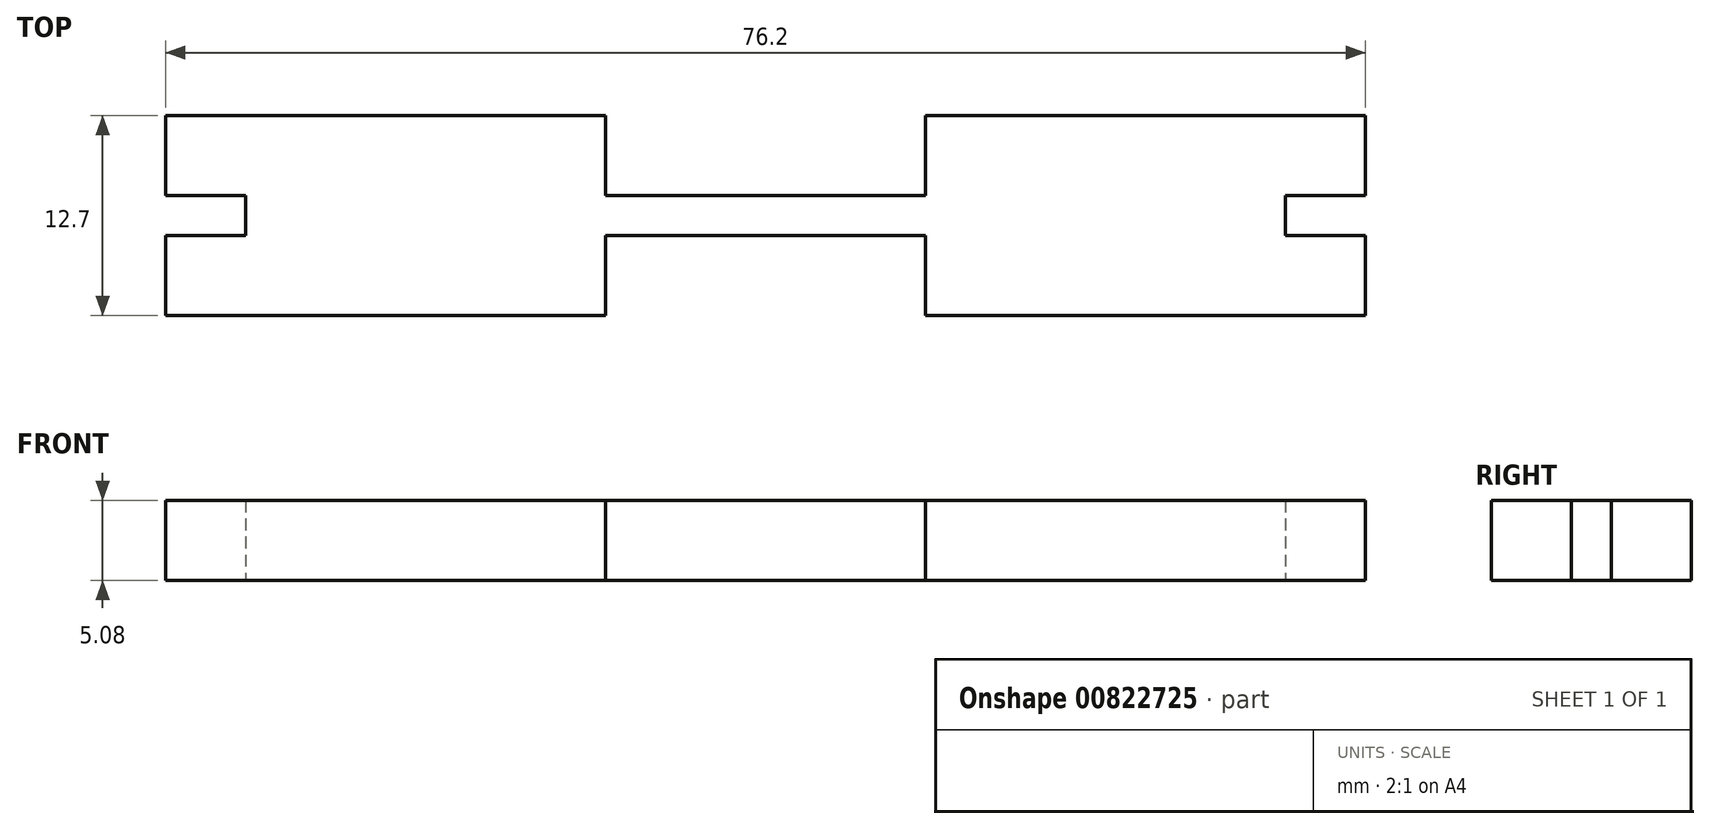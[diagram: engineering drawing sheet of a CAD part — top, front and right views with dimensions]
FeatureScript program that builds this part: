
annotation { "Feature Type Name" : "Feature", "Feature Type Description" : "" }
export const myFeature = defineFeature(function(context is Context, id is Id, definition is map)
    precondition{}
    {
        {
            var Q0;
            Q0=qCreatedBy(makeId("Top.planeOp"),FACE);
            var sketch = newSketch(context, id + "F0", { "sketchPlane" : qUnion([Q0])});
            skLineSegment(sketch, "E0.top", {"start": v(0, -12.7) * mm, "end": v(27.94, -12.7) * mm});
            skLineSegment(sketch, "E0.left", {"start": v(0, 0) * mm, "end": v(0, -5.08) * mm});
            skLineSegment(sketch, "E1", {"start": v(27.94, -12.7) * mm, "end": v(27.94, -7.62) * mm});
            skLineSegment(sketch, "E2", {"start": v(27.94, -7.62) * mm, "end": v(48.26, -7.62) * mm});
            skLineSegment(sketch, "E3", {"start": v(48.26, -7.62) * mm, "end": v(48.26, -12.7) * mm});
            skLineSegment(sketch, "E4", {"start": v(48.26, -12.7) * mm, "end": v(76.2, -12.7) * mm});
            skLineSegment(sketch, "E5", {"start": v(0, -12.7) * mm, "end": v(0, -7.62) * mm});
            skLineSegment(sketch, "E6", {"start": v(0, -7.62) * mm, "end": v(5.08, -7.62) * mm});
            skLineSegment(sketch, "E7", {"start": v(5.08, -7.62) * mm, "end": v(5.08, -5.08) * mm});
            skLineSegment(sketch, "E8", {"start": v(5.08, -5.08) * mm, "end": v(0, -5.08) * mm});
            skLineSegment(sketch, "E9.trimOffspring", {"start": v(0, -7.62) * mm, "end": v(0, -12.7) * mm});
            skLineSegment(sketch, "E10", {"start": v(5.08, -6.35) * mm, "end": v(7.44, -6.35) * mm, "construction": true});
            skLineSegment(sketch, "E11", {"start": v(38.1, -7.62) * mm, "end": v(38.1, 0) * mm, "construction": true});
            skLineSegment(sketch, "E12.MirrorCS", {"start": v(48.26, -7.62) * mm, "end": v(27.94, -7.62) * mm});
            skLineSegment(sketch, "E13.MirrorCS", {"start": v(76.2, -7.62) * mm, "end": v(76.2, -12.7) * mm});
            skLineSegment(sketch, "E14.MirrorCS", {"start": v(76.2, -7.62) * mm, "end": v(71.12, -7.62) * mm});
            skLineSegment(sketch, "E15.MirrorCS", {"start": v(71.12, -7.62) * mm, "end": v(71.12, -5.08) * mm});
            skLineSegment(sketch, "E16.MirrorCS", {"start": v(71.12, -5.08) * mm, "end": v(76.2, -5.08) * mm});
            skLineSegment(sketch, "E17.MirrorCS", {"start": v(76.2, 0) * mm, "end": v(76.2, -5.08) * mm});
            skLineSegment(sketch, "E18.MirrorCS", {"start": v(0, 0) * mm, "end": v(27.94, 0) * mm});
            skLineSegment(sketch, "E19.MirrorCS", {"start": v(27.94, 0) * mm, "end": v(27.94, -5.08) * mm});
            skLineSegment(sketch, "E20.MirrorCS", {"start": v(48.26, -5.08) * mm, "end": v(27.94, -5.08) * mm});
            skLineSegment(sketch, "E21.MirrorCS", {"start": v(48.26, -5.08) * mm, "end": v(48.26, 0) * mm});
            skLineSegment(sketch, "E22.MirrorCS", {"start": v(48.26, 0) * mm, "end": v(76.2, 0) * mm});
            skSolve(sketch);
        }
        {
            var Q0;
            Q0=makeQuery(id+"F0.imprint","IMPRINT",FACE,{"disambiguationData":[TD([[makeQuery(id+"F0.imprint","IMPRINT",EDGE,{"derivedFrom":sQuery(id+"F0.wireOp",EDGE,"E0.left")}),1.0]])]});
            extrude(context, id + "F1", {"entities" : qUnion([Q0]), "depth" : 5.08 * mm, "offsetDistance" : 25.4 * mm});
        }
    });
